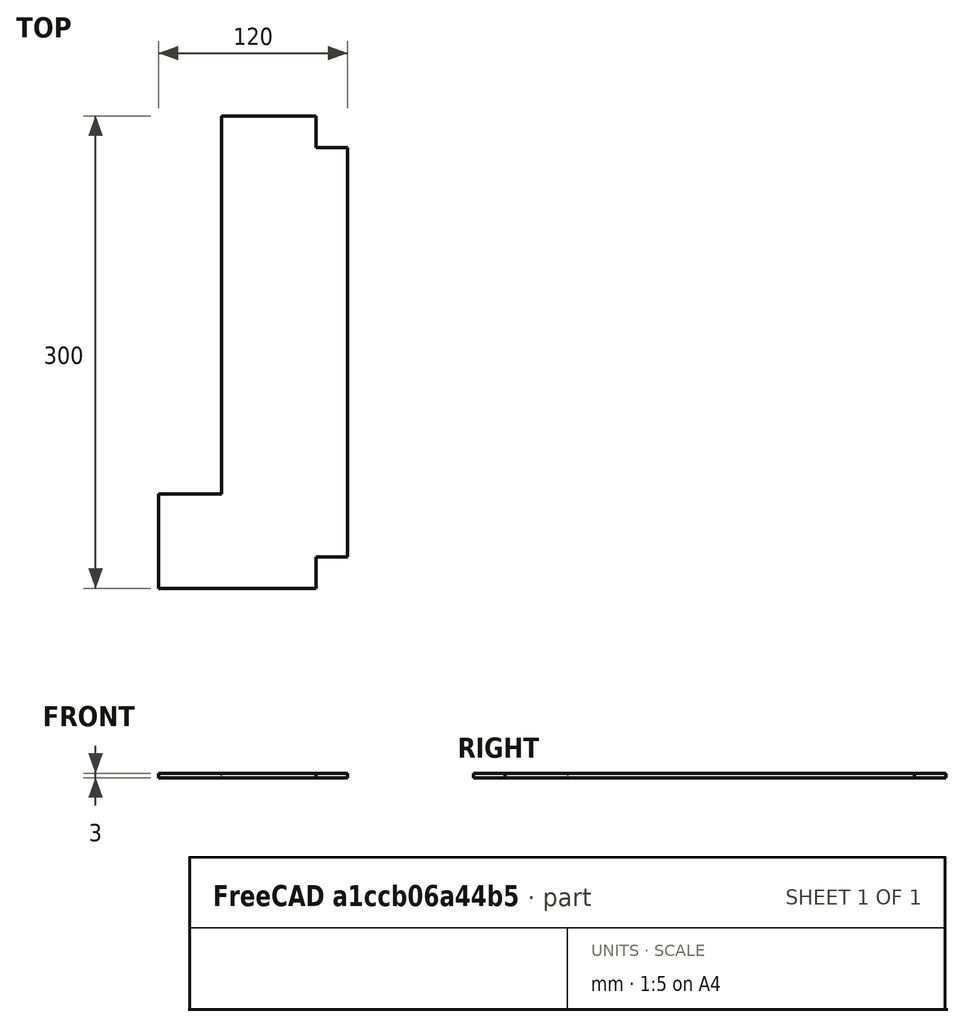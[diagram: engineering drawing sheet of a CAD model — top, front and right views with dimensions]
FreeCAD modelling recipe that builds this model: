
FCSTD DOCUMENT  (FreeCAD 0.18R)
Label: Coroplast-Bottom-Right-Front
License: CreativeCommons Attribution
LicenseURL: http://creativecommons.org/licenses/by/4.0/
objects: Drawing::FeatureViewPython×9, Sketcher::SketchObject×1, PartDesign::Pad×1, PartDesign::Body×1, App::Part×1, Drawing::FeatureViewPart×1, Drawing::FeaturePage×1
note: 4 computed .brp shape members not serialized (recipe doc carries the construction recipe); baked Part::Feature solids carry a one-line shape summary decoded from their .brp

FEATURE [Sketcher::SketchObject] Sketch
  MapMode = 5
  Support = -> [XY_Plane]
  sketch-geometry (10):
    g0: LineSegment StartX=35 StartY=-15 StartZ=0 EndX=35 EndY=-75 EndZ=0
    g1: LineSegment StartX=35 StartY=-75 StartZ=0 EndX=135 EndY=-75 EndZ=0
    g2: LineSegment StartX=135 StartY=-55 StartZ=0 EndX=155 EndY=-55 EndZ=0
    g3: LineSegment StartX=155 StartY=-55 StartZ=0 EndX=155 EndY=205 EndZ=0
    g4: LineSegment StartX=155 StartY=205 StartZ=0 EndX=135 EndY=205 EndZ=0
    g5: LineSegment StartX=135 StartY=225 StartZ=0 EndX=75 EndY=225 EndZ=0
    g6: LineSegment StartX=75 StartY=225 StartZ=0 EndX=75 EndY=-15 EndZ=0
    g7: LineSegment StartX=75 StartY=-15 StartZ=0 EndX=35 EndY=-15 EndZ=0
    g8: LineSegment StartX=135 StartY=225 StartZ=0 EndX=135 EndY=205 EndZ=0
    g9: LineSegment StartX=135 StartY=-55 StartZ=0 EndX=135 EndY=-75 EndZ=0
  constraints (30):
    c: Coincident(g0,g1)
    c: Coincident(g2,g3)
    c: Coincident(g3,g4)
    c: Coincident(g5,g6)
    c: Coincident(g6,g7)
    c: Coincident(g7,g0)
    c: Vertical(g0)
    c: Vertical(g6)
    c: Vertical(g3)
    c: Horizontal(g5)
    c: Horizontal(g2)
    c: Horizontal(g7)
    c: Horizontal(g1)
    c: DistanceX(g2,g2) = 20
    c: Vertical(g2,g4)
    c: Horizontal(g4)
    c: DistanceY(g3,g3) = 260
    c: Coincident(g5,g8)
    c: Coincident(g8,g4)
    c: Vertical(g8)
    c: Coincident(g2,g9)
    c: Coincident(g1,g9)
    c: Vertical(g9)
    c: DistanceY(g9,g9) = 20
    c: DistanceY(g1,g5) = 300
    c: DistanceX(g0,g2) = 120
    c: DistanceY(g0,g0) = 60
    c: DistanceY(g6,g-1) = 15
    c: DistanceX(g-1,g0) = 35
    c: DistanceX(g5,g3) = 80
FEATURE [PartDesign::Pad] Pad
  Length = 3
  Length2 = 100
  Profile = -> Sketch
  Type = 0
FEATURE [PartDesign::Body] Body  label="BottomSheetRightFront"
  Group = -> [Sketch,Pad]
  Origin = -> Origin
  Tip = -> Pad
FEATURE [App::Part] Part
  Group = -> [Body]
  Origin = -> Origin001
FEATURE [Drawing::FeatureViewPart] View
  Direction = (0,0,1)
  HiddenWidth = 0.15
  LineWidth = 0.35
  Rotation = 0
  Scale = 0.5
  ShowHiddenLines = false
  ShowSmoothLines = false
  Source = -> Body
  Tolerance = 0.05
  ViewResult = <g id="View"\n   transform="rotate(0,70,180) translate(70,180) scale(0.5,0.5)"\n  >\n<g   fill="none"\n   stroke="rgb(0, 0, 0)"\n   stroke-linecap="butt"\n   stroke-linejoin="miter"\n   stroke-width="0.700000"\n   transform="scale(1,-1)"\n  >\n<path id= "1" d=" M 135 225 L 75 225 " />\n<path id= "2" d=" M 75 225 L 75 -15 " />\n<path id= "3" d=" M 75 -15 L 35 -15 " />\n<path id= "4" d=" M 35 -15 L 35 -75 " />\n<path id= "5" d=" M 35 -75 L 135 -75 " />\n<path id= "6" d=" M 135 -55 L 135 -75 " />\n<path id= "7" d=" M 135 -55 L 155 -55 " />\n<path id= "8" d=" M 155 -55 L 155 205 " />\n<path id= "9" d=" M 155 205 L 135 205 " />\n<path id= "10" d=" M 135 225 L 135 205 " />\n</g>\n</g>
  Visible = true
  X = 70
  Y = 180
FEATURE [Drawing::FeatureViewPython] dim001  # drawing view (typed FeaturePython)
  Rotation = 0
  ViewResult = <g> \n  <line x1="87.500000" y1="219.500000" x2="87.500000" y2="233.553095" style="stroke:rgb(0,0,255);stroke-width:0.50" />\n<line x1="147.500000" y1="209.500000" x2="147.500000" y2="233.553095" style="stroke:rgb(0,0,255);stroke-width:0.50" />\n<line x1="87.500000" y1="232.553095" x2="147.500000" y2="232.553095" style="stroke:rgb(0,0,255);stroke-width:0.50" /> \n  <polygon points="147.500000,232.553095 144.500000,231.553095 143.500000,232.553095 144.500000,233.553095" style="fill:rgb(0,0,255);stroke:rgb(0,0,255);stroke-width:0" /><polygon points="87.500000,232.553095 90.500000,233.553095 91.500000,232.553095 90.500000,231.553095" style="fill:rgb(0,0,255);stroke:rgb(0,0,255);stroke-width:0" /> \n  <text x="117.500000" y="230.553095" font-family="inherit" font-size="3.6" fill="rgb(0,0,255)" text-anchor="middle" transform="rotate(0.000000 117.500000,230.553095)" >120</text> </g>
  Visible = true
  X = 0
  Y = 0
  arrowL1 = 3
  arrowL2 = 1
  arrowW = 2
  arrow_scheme = 0
  autoPlaceOffset = 2
  autoPlaceText = true
  click1_x = 143.45
  click1_y = 232.553
  click2_x = 143.45
  click2_y = 232.553
  comma_decimal_place = false
  dimension_line_overshoot = 1
  gap_datum_points = 2
  halfDimension_linear = false
  lineColor = rgb(0,0,255)
  strokeWidth = 0.5
  textFormat_linear = %(value)3.3f
  textRenderer_color = rgb(0,0,255)
  textRenderer_family = inherit
  textRenderer_size = 3.6
  unit_custom_scale = 1
  unit_scheme = 0
FEATURE [Drawing::FeatureViewPython] dim002  # drawing view (typed FeaturePython)
  Rotation = 0
  ViewResult = <g> \n  <line x1="147.500000" y1="209.500000" x2="147.500000" y2="224.713677" style="stroke:rgb(0,0,255);stroke-width:0.50" />\n<line x1="137.500000" y1="219.500000" x2="137.500000" y2="224.713677" style="stroke:rgb(0,0,255);stroke-width:0.50" />\n<line x1="147.500000" y1="223.713677" x2="137.500000" y2="223.713677" style="stroke:rgb(0,0,255);stroke-width:0.50" /> \n  <polygon points="137.500000,223.713677 134.500000,222.713677 133.500000,223.713677 134.500000,224.713677" style="fill:rgb(0,0,255);stroke:rgb(0,0,255);stroke-width:0" /><polygon points="147.500000,223.713677 150.500000,224.713677 151.500000,223.713677 150.500000,222.713677" style="fill:rgb(0,0,255);stroke:rgb(0,0,255);stroke-width:0" /> \n  <text x="142.500000" y="221.713677" font-family="inherit" font-size="3.6" fill="rgb(0,0,255)" text-anchor="middle" transform="rotate(0.000000 142.500000,221.713677)" >20</text> </g>
  Visible = true
  X = 0
  Y = 0
  arrowL1 = 3
  arrowL2 = 1
  arrowW = 2
  arrow_scheme = 0
  autoPlaceOffset = 2
  autoPlaceText = true
  click1_x = 140.667
  click1_y = 223.714
  click2_x = 140.667
  click2_y = 223.714
  comma_decimal_place = false
  dimension_line_overshoot = 1
  gap_datum_points = 2
  halfDimension_linear = false
  lineColor = rgb(0,0,255)
  strokeWidth = 0.5
  textFormat_linear = %(value)3.3f
  textRenderer_color = rgb(0,0,255)
  textRenderer_family = inherit
  textRenderer_size = 3.6
  unit_custom_scale = 1
  unit_scheme = 0
FEATURE [Drawing::FeatureViewPython] dim003  # drawing view (typed FeaturePython)
  Rotation = 0
  ViewResult = <g> \n  <line x1="135.500000" y1="207.500000" x2="126.844182" y2="207.500000" style="stroke:rgb(0,0,255);stroke-width:0.50" />\n<line x1="135.500000" y1="217.500000" x2="126.844182" y2="217.500000" style="stroke:rgb(0,0,255);stroke-width:0.50" />\n<line x1="127.844182" y1="207.500000" x2="127.844182" y2="217.500000" style="stroke:rgb(0,0,255);stroke-width:0.50" /> \n  <polygon points="127.844182,217.500000 126.844182,220.500000 127.844182,221.500000 128.844182,220.500000" style="fill:rgb(0,0,255);stroke:rgb(0,0,255);stroke-width:0" /><polygon points="127.844182,207.500000 128.844182,204.500000 127.844182,203.500000 126.844182,204.500000" style="fill:rgb(0,0,255);stroke:rgb(0,0,255);stroke-width:0" /> \n  <text x="125.844182" y="212.500000" font-family="inherit" font-size="3.6" fill="rgb(0,0,255)" text-anchor="middle" transform="rotate(-90.000000 125.844182,212.500000)" >20</text> </g>
  Visible = true
  X = 0
  Y = 0
  arrowL1 = 3
  arrowL2 = 1
  arrowW = 2
  arrow_scheme = 0
  autoPlaceOffset = 2
  autoPlaceText = true
  click1_x = 127.844
  click1_y = 216.347
  click2_x = 127.844
  click2_y = 216.347
  comma_decimal_place = false
  dimension_line_overshoot = 1
  gap_datum_points = 2
  halfDimension_linear = false
  lineColor = rgb(0,0,255)
  strokeWidth = 0.5
  textFormat_linear = %(value)3.3f
  textRenderer_color = rgb(0,0,255)
  textRenderer_family = inherit
  textRenderer_size = 3.6
  unit_custom_scale = 1
  unit_scheme = 0
FEATURE [Drawing::FeatureViewPython] dim004  # drawing view (typed FeaturePython)
  Rotation = 0
  ViewResult = <g> \n  <line x1="85.500000" y1="187.500000" x2="69.988169" y2="187.500000" style="stroke:rgb(0,0,255);stroke-width:0.50" />\n<line x1="85.500000" y1="217.500000" x2="69.988169" y2="217.500000" style="stroke:rgb(0,0,255);stroke-width:0.50" />\n<line x1="70.988169" y1="187.500000" x2="70.988169" y2="217.500000" style="stroke:rgb(0,0,255);stroke-width:0.50" /> \n  <polygon points="70.988169,217.500000 71.988169,214.500000 70.988169,213.500000 69.988169,214.500000" style="fill:rgb(0,0,255);stroke:rgb(0,0,255);stroke-width:0" /><polygon points="70.988169,187.500000 69.988169,190.500000 70.988169,191.500000 71.988169,190.500000" style="fill:rgb(0,0,255);stroke:rgb(0,0,255);stroke-width:0" /> \n  <text x="68.988169" y="202.500000" font-family="inherit" font-size="3.6" fill="rgb(0,0,255)" text-anchor="middle" transform="rotate(-90.000000 68.988169,202.500000)" >60</text> </g>
  Visible = true
  X = 0
  Y = 0
  arrowL1 = 3
  arrowL2 = 1
  arrowW = 2
  arrow_scheme = 0
  autoPlaceOffset = 2
  autoPlaceText = true
  click1_x = 70.9882
  click1_y = 211.273
  click2_x = 70.9882
  click2_y = 211.273
  comma_decimal_place = false
  dimension_line_overshoot = 1
  gap_datum_points = 2
  halfDimension_linear = false
  lineColor = rgb(0,0,255)
  strokeWidth = 0.5
  textFormat_linear = %(value)3.3f
  textRenderer_color = rgb(0,0,255)
  textRenderer_family = inherit
  textRenderer_size = 3.6
  unit_custom_scale = 1
  unit_scheme = 0
FEATURE [Drawing::FeatureViewPython] dim006  # drawing view (typed FeaturePython)
  Rotation = 0
  ViewResult = <g> \n  <line x1="89.500000" y1="217.500000" x2="182.176115" y2="217.500000" style="stroke:rgb(0,0,255);stroke-width:0.50" />\n<line x1="119.500000" y1="67.500000" x2="182.176115" y2="67.500000" style="stroke:rgb(0,0,255);stroke-width:0.50" />\n<line x1="181.176115" y1="217.500000" x2="181.176115" y2="67.500000" style="stroke:rgb(0,0,255);stroke-width:0.50" /> \n  <polygon points="181.176115,67.500000 180.176115,70.500000 181.176115,71.500000 182.176115,70.500000" style="fill:rgb(0,0,255);stroke:rgb(0,0,255);stroke-width:0" /><polygon points="181.176115,217.500000 182.176115,214.500000 181.176115,213.500000 180.176115,214.500000" style="fill:rgb(0,0,255);stroke:rgb(0,0,255);stroke-width:0" /> \n  <text x="179.176115" y="142.500000" font-family="inherit" font-size="3.6" fill="rgb(0,0,255)" text-anchor="middle" transform="rotate(-90.000000 179.176115,142.500000)" >300</text> </g>
  Visible = true
  X = 0
  Y = 0
  arrowL1 = 3
  arrowL2 = 1
  arrowW = 2
  arrow_scheme = 0
  autoPlaceOffset = 2
  autoPlaceText = true
  click1_x = 181.176
  click1_y = 82.4416
  click2_x = 181.176
  click2_y = 82.4416
  comma_decimal_place = false
  dimension_line_overshoot = 1
  gap_datum_points = 2
  halfDimension_linear = false
  lineColor = rgb(0,0,255)
  strokeWidth = 0.5
  textFormat_linear = %(value)3.3f
  textRenderer_color = rgb(0,0,255)
  textRenderer_family = inherit
  textRenderer_size = 3.6
  unit_custom_scale = 1
  unit_scheme = 0
FEATURE [Drawing::FeatureViewPython] dim007  # drawing view (typed FeaturePython)
  Rotation = 0
  ViewResult = <g> \n  <line x1="147.500000" y1="79.500000" x2="147.500000" y2="89.632920" style="stroke:rgb(0,0,255);stroke-width:0.50" />\n<line x1="137.500000" y1="79.500000" x2="137.500000" y2="89.632920" style="stroke:rgb(0,0,255);stroke-width:0.50" />\n<line x1="147.500000" y1="88.632920" x2="137.500000" y2="88.632920" style="stroke:rgb(0,0,255);stroke-width:0.50" /> \n  <polygon points="137.500000,88.632920 134.500000,87.632920 133.500000,88.632920 134.500000,89.632920" style="fill:rgb(0,0,255);stroke:rgb(0,0,255);stroke-width:0" /><polygon points="147.500000,88.632920 150.500000,89.632920 151.500000,88.632920 150.500000,87.632920" style="fill:rgb(0,0,255);stroke:rgb(0,0,255);stroke-width:0" /> \n  <text x="142.500000" y="86.632920" font-family="inherit" font-size="3.6" fill="rgb(0,0,255)" text-anchor="middle" transform="rotate(0.000000 142.500000,86.632920)" >20</text> </g>
  Visible = true
  X = 0
  Y = 0
  arrowL1 = 3
  arrowL2 = 1
  arrowW = 2
  arrow_scheme = 0
  autoPlaceOffset = 2
  autoPlaceText = true
  click1_x = 144.191
  click1_y = 88.6329
  click2_x = 144.191
  click2_y = 88.6329
  comma_decimal_place = false
  dimension_line_overshoot = 1
  gap_datum_points = 2
  halfDimension_linear = false
  lineColor = rgb(0,0,255)
  strokeWidth = 0.5
  textFormat_linear = %(value)3.3f
  textRenderer_color = rgb(0,0,255)
  textRenderer_family = inherit
  textRenderer_size = 3.6
  unit_custom_scale = 1
  unit_scheme = 0
FEATURE [Drawing::FeatureViewPython] dim008  # drawing view (typed FeaturePython)
  Rotation = 0
  ViewResult = <g> \n  <line x1="135.500000" y1="67.500000" x2="127.224463" y2="67.500000" style="stroke:rgb(0,0,255);stroke-width:0.50" />\n<line x1="135.500000" y1="77.500000" x2="127.224463" y2="77.500000" style="stroke:rgb(0,0,255);stroke-width:0.50" />\n<line x1="128.224463" y1="67.500000" x2="128.224463" y2="77.500000" style="stroke:rgb(0,0,255);stroke-width:0.50" /> \n  <polygon points="128.224463,77.500000 127.224463,80.500000 128.224463,81.500000 129.224463,80.500000" style="fill:rgb(0,0,255);stroke:rgb(0,0,255);stroke-width:0" /><polygon points="128.224463,67.500000 129.224463,64.500000 128.224463,63.500000 127.224463,64.500000" style="fill:rgb(0,0,255);stroke:rgb(0,0,255);stroke-width:0" /> \n  <text x="126.224463" y="72.500000" font-family="inherit" font-size="3.6" fill="rgb(0,0,255)" text-anchor="middle" transform="rotate(-90.000000 126.224463,72.500000)" >20</text> </g>
  Visible = true
  X = 0
  Y = 0
  arrowL1 = 3
  arrowL2 = 1
  arrowW = 2
  arrow_scheme = 0
  autoPlaceOffset = 2
  autoPlaceText = true
  click1_x = 128.224
  click1_y = 73.4806
  click2_x = 128.224
  click2_y = 73.4806
  comma_decimal_place = false
  dimension_line_overshoot = 1
  gap_datum_points = 2
  halfDimension_linear = false
  lineColor = rgb(0,0,255)
  strokeWidth = 0.5
  textFormat_linear = %(value)3.3f
  textRenderer_color = rgb(0,0,255)
  textRenderer_family = inherit
  textRenderer_size = 3.6
  unit_custom_scale = 1
  unit_scheme = 0
FEATURE [Drawing::FeatureViewPython] dim009  # drawing view (typed FeaturePython)
  Rotation = 0
  ViewResult = <g> \n  <line x1="115.500000" y1="67.500000" x2="103.436951" y2="67.500000" style="stroke:rgb(0,0,255);stroke-width:0.50" />\n<line x1="115.500000" y1="187.500000" x2="103.436951" y2="187.500000" style="stroke:rgb(0,0,255);stroke-width:0.50" />\n<line x1="104.436951" y1="67.500000" x2="104.436951" y2="187.500000" style="stroke:rgb(0,0,255);stroke-width:0.50" /> \n  <polygon points="104.436951,187.500000 105.436951,184.500000 104.436951,183.500000 103.436951,184.500000" style="fill:rgb(0,0,255);stroke:rgb(0,0,255);stroke-width:0" /><polygon points="104.436951,67.500000 103.436951,70.500000 104.436951,71.500000 105.436951,70.500000" style="fill:rgb(0,0,255);stroke:rgb(0,0,255);stroke-width:0" /> \n  <text x="102.436951" y="127.500000" font-family="inherit" font-size="3.6" fill="rgb(0,0,255)" text-anchor="middle" transform="rotate(-90.000000 102.436951,127.500000)" >240</text> </g>
  Visible = true
  X = 0
  Y = 0
  arrowL1 = 3
  arrowL2 = 1
  arrowW = 2
  arrow_scheme = 0
  autoPlaceOffset = 2
  autoPlaceText = true
  click1_x = 104.437
  click1_y = 141.748
  click2_x = 104.437
  click2_y = 141.748
  comma_decimal_place = false
  dimension_line_overshoot = 1
  gap_datum_points = 2
  halfDimension_linear = false
  lineColor = rgb(0,0,255)
  strokeWidth = 0.5
  textFormat_linear = %(value)3.3f
  textRenderer_color = rgb(0,0,255)
  textRenderer_family = inherit
  textRenderer_size = 3.6
  unit_custom_scale = 1
  unit_scheme = 0
FEATURE [Drawing::FeatureViewPython] dim005  # drawing view (typed FeaturePython)
  Rotation = 0
  ViewResult = <g> \n  <line x1="87.500000" y1="189.500000" x2="87.500000" y2="201.401638" style="stroke:rgb(0,0,255);stroke-width:0.50" />\n<line x1="107.500000" y1="189.500000" x2="107.500000" y2="201.401638" style="stroke:rgb(0,0,255);stroke-width:0.50" />\n<line x1="87.500000" y1="200.401638" x2="107.500000" y2="200.401638" style="stroke:rgb(0,0,255);stroke-width:0.50" /> \n  <polygon points="107.500000,200.401638 104.500000,199.401638 103.500000,200.401638 104.500000,201.401638" style="fill:rgb(0,0,255);stroke:rgb(0,0,255);stroke-width:0" /><polygon points="87.500000,200.401638 90.500000,201.401638 91.500000,200.401638 90.500000,199.401638" style="fill:rgb(0,0,255);stroke:rgb(0,0,255);stroke-width:0" /> \n  <text x="97.500000" y="198.401638" font-family="inherit" font-size="3.6" fill="rgb(0,0,255)" text-anchor="middle" transform="rotate(0.000000 97.500000,198.401638)" >40</text> </g>
  Visible = true
  X = 0
  Y = 0
  arrowL1 = 3
  arrowL2 = 1
  arrowW = 2
  arrow_scheme = 0
  autoPlaceOffset = 2
  autoPlaceText = true
  click1_x = 105.968
  click1_y = 200.402
  click2_x = 105.968
  click2_y = 200.402
  comma_decimal_place = false
  dimension_line_overshoot = 1
  gap_datum_points = 2
  halfDimension_linear = false
  lineColor = rgb(0,0,255)
  strokeWidth = 0.5
  textFormat_linear = %(value)3.3f
  textRenderer_color = rgb(0,0,255)
  textRenderer_family = inherit
  textRenderer_size = 3.6
  unit_custom_scale = 1
  unit_scheme = 0
FEATURE [Drawing::FeaturePage] Page
  Group = -> [View,dim001,dim002,dim003,dim004,dim006,dim007,dim008,dim009,dim005]
  Template = <path>
note: 1 file-system path scrubbed to <path> (originals preserved in the JSON sidecar)
